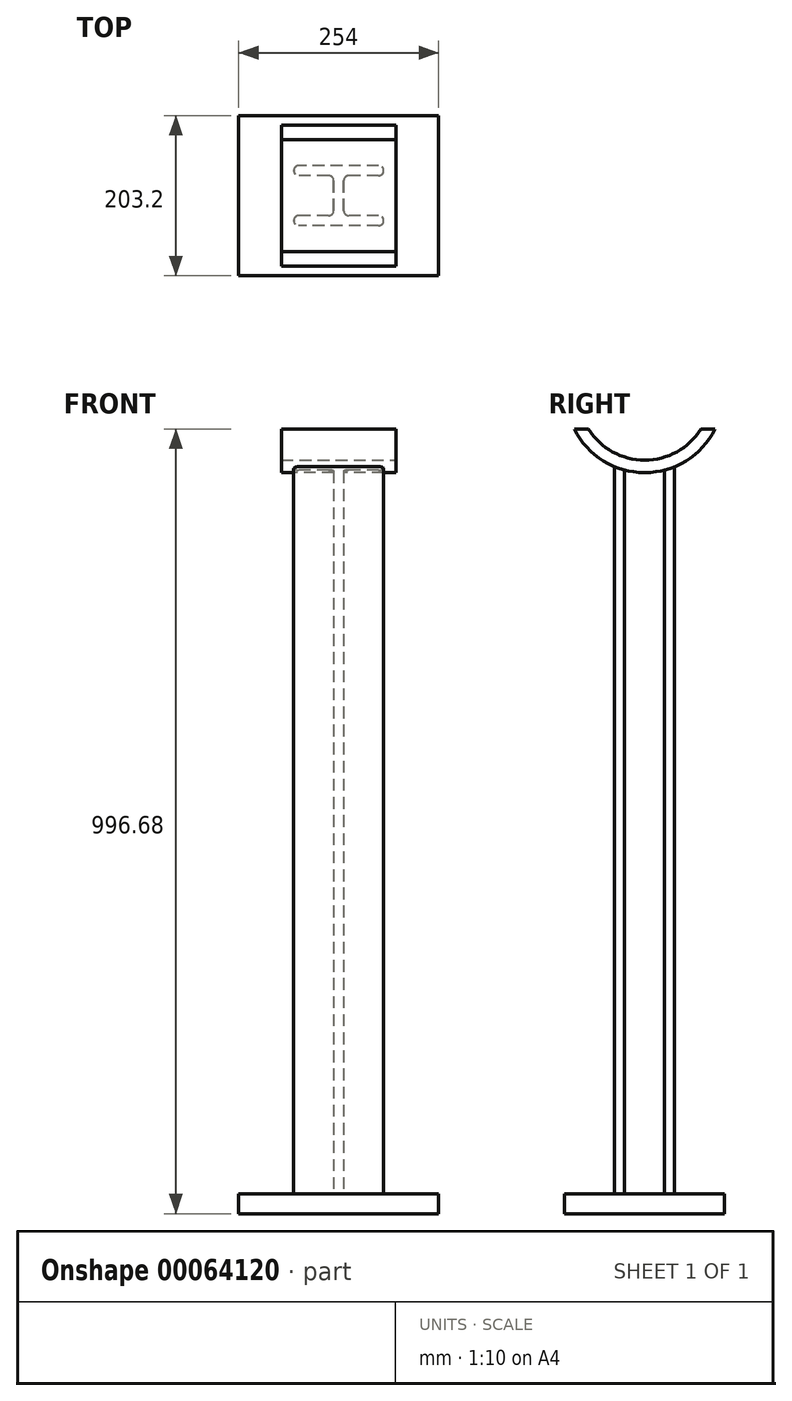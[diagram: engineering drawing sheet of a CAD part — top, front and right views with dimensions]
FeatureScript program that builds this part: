
annotation { "Feature Type Name" : "Feature", "Feature Type Description" : "" }
export const myFeature = defineFeature(function(context is Context, id is Id, definition is map)
    precondition{}
    {
        {
            var Q0;
            Q0=qCreatedBy(makeId("Top.planeOp"),FACE);
            var sketch = newSketch(context, id + "F0", { "sketchPlane" : qUnion([Q0])});
            skLineSegment(sketch, "E0.bottom", {"start": v(50.8, 38.1) * mm, "end": v(-50.8, 38.1) * mm});
            skLineSegment(sketch, "E0.top", {"start": v(50.8, -38.1) * mm, "end": v(-50.8, -38.1) * mm});
            skLineSegment(sketch, "E0.left", {"start": v(57.15, 31.75) * mm, "end": v(57.15, 31.75) * mm});
            skLineSegment(sketch, "E0.right", {"start": v(-57.15, 31.75) * mm, "end": v(-57.15, 31.75) * mm});
            skPoint(sketch, "E0.middle", {"position": v(0, 0) * mm});
            skLineSegment(sketch, "E1", {"start": v(-50.8, 25.4) * mm, "end": v(-12.7, 25.4) * mm});
            skLineSegment(sketch, "E2", {"start": v(-50.8, -25.4) * mm, "end": v(-12.7, -25.4) * mm});
            skLineSegment(sketch, "E3", {"start": v(-6.35, 19.05) * mm, "end": v(-6.35, -19.05) * mm});
            skLineSegment(sketch, "E4", {"start": v(6.35, 19.05) * mm, "end": v(6.35, -19.05) * mm});
            skLineSegment(sketch, "E5.trimOffspring", {"start": v(12.7, 25.4) * mm, "end": v(50.8, 25.4) * mm});
            skLineSegment(sketch, "E6.trimOffspring", {"start": v(-57.15, -31.75) * mm, "end": v(-57.15, -31.75) * mm});
            skLineSegment(sketch, "E7.trimOffspring", {"start": v(57.15, -31.75) * mm, "end": v(57.15, -31.75) * mm});
            skLineSegment(sketch, "E8.trimOffspring", {"start": v(12.7, -25.4) * mm, "end": v(50.8, -25.4) * mm});
            skPoint(sketch, "E9.visualSharp", {"position": v(-6.35, 25.4) * mm});
            skArc(sketch, "E9.filletArc", {"start": v(-6.35, 19.05) * mm, "mid": v(-8.2, 23.54) * mm, "end": v(-12.7, 25.4) * mm});
            skPoint(sketch, "E10.visualSharp", {"position": v(6.35, 25.4) * mm});
            skArc(sketch, "E10.filletArc", {"start": v(12.7, 25.4) * mm, "mid": v(8.2, 23.54) * mm, "end": v(6.35, 19.05) * mm});
            skPoint(sketch, "E11.visualSharp", {"position": v(-6.35, -25.4) * mm});
            skArc(sketch, "E11.filletArc", {"start": v(-12.7, -25.4) * mm, "mid": v(-8.2, -23.54) * mm, "end": v(-6.35, -19.05) * mm});
            skPoint(sketch, "E12.visualSharp", {"position": v(6.35, -25.4) * mm});
            skArc(sketch, "E12.filletArc", {"start": v(6.35, -19.05) * mm, "mid": v(8.2, -23.54) * mm, "end": v(12.7, -25.4) * mm});
            skPoint(sketch, "E13.visualSharp", {"position": v(-57.15, 25.4) * mm});
            skArc(sketch, "E13.filletArc", {"start": v(-57.15, 31.75) * mm, "mid": v(-55.3, 27.26) * mm, "end": v(-50.8, 25.4) * mm});
            skPoint(sketch, "E14.visualSharp", {"position": v(-57.15, 38.1) * mm});
            skArc(sketch, "E14.filletArc", {"start": v(-50.8, 38.1) * mm, "mid": v(-55.3, 36.24) * mm, "end": v(-57.15, 31.75) * mm});
            skPoint(sketch, "E15.visualSharp", {"position": v(57.15, 38.1) * mm});
            skArc(sketch, "E15.filletArc", {"start": v(57.15, 31.75) * mm, "mid": v(55.3, 36.24) * mm, "end": v(50.8, 38.1) * mm});
            skPoint(sketch, "E16.visualSharp", {"position": v(57.15, 25.4) * mm});
            skArc(sketch, "E16.filletArc", {"start": v(50.8, 25.4) * mm, "mid": v(55.3, 27.26) * mm, "end": v(57.15, 31.75) * mm});
            skPoint(sketch, "E17.visualSharp", {"position": v(57.15, -25.4) * mm});
            skArc(sketch, "E17.filletArc", {"start": v(57.15, -31.75) * mm, "mid": v(55.3, -27.26) * mm, "end": v(50.8, -25.4) * mm});
            skPoint(sketch, "E18.visualSharp", {"position": v(57.15, -38.1) * mm});
            skArc(sketch, "E18.filletArc", {"start": v(50.8, -38.1) * mm, "mid": v(55.3, -36.24) * mm, "end": v(57.15, -31.75) * mm});
            skPoint(sketch, "E19.visualSharp", {"position": v(-57.15, -38.1) * mm});
            skArc(sketch, "E19.filletArc", {"start": v(-57.15, -31.75) * mm, "mid": v(-55.3, -36.24) * mm, "end": v(-50.8, -38.1) * mm});
            skPoint(sketch, "E20.visualSharp", {"position": v(-57.15, -25.4) * mm});
            skArc(sketch, "E20.filletArc", {"start": v(-50.8, -25.4) * mm, "mid": v(-55.3, -27.26) * mm, "end": v(-57.15, -31.75) * mm});
            skSolve(sketch);
        }
        {
            var Q0;
            Q0=qCreatedBy(makeId("Top.planeOp"),FACE);
            var sketch = newSketch(context, id + "F1", { "sketchPlane" : qUnion([Q0])});
            skLineSegment(sketch, "E21.bottom", {"start": v(127, 101.6) * mm, "end": v(-127, 101.6) * mm});
            skLineSegment(sketch, "E21.top", {"start": v(127, -101.6) * mm, "end": v(-127, -101.6) * mm});
            skLineSegment(sketch, "E21.left", {"start": v(127, 101.6) * mm, "end": v(127, -101.6) * mm});
            skLineSegment(sketch, "E21.right", {"start": v(-127, 101.6) * mm, "end": v(-127, -101.6) * mm});
            skPoint(sketch, "E21.middle", {"position": v(0, 0) * mm});
            skSolve(sketch);
        }
        {
            var Q0;
            Q0=makeQuery(id+"F1.imprint","IMPRINT",FACE,{"disambiguationData":[TD([[makeQuery(id+"F1.imprint","IMPRINT",EDGE,{"derivedFrom":sQuery(id+"F1.wireOp",EDGE,"E21.bottom")}),1.0]])]});
            extrude(context, id + "F2", {"entities" : qUnion([Q0]), "oppositeDirection" : true, "depth" : 25.4 * mm, "offsetDistance" : 25.4 * mm});
        }
        {
            var Q0;
            Q0 = qSketchRegion(id + "F0", true);
            extrude(context, id + "F3", {"entities" : qUnion([Q0]), "operationType" : NewBodyOperationType.ADD, "depth" : 1019.05 * mm, "offsetDistance" : 25.4 * mm});
        }
        {
            var Q0;
            Q0=qCreatedBy(makeId("Right.planeOp"),FACE);
            var sketch = newSketch(context, id + "F4", { "sketchPlane" : qUnion([Q0])});
            skLineSegment(sketch, "E22", {"start": v(0, 0) * mm, "end": v(0, 1016) * mm, "construction": true});
            skCircle(sketch, "E23", {"center": v(0, 1016) * mm, "radius": 84.14 * mm});
            skArc(sketch, "E24", {"start": v(-89.4, 971.28) * mm, "mid": v(0, 916.03) * mm, "end": v(89.4, 971.28) * mm});
            skLineSegment(sketch, "E25", {"start": v(-89.4, 971.28) * mm, "end": v(-71.27, 971.28) * mm});
            skLineSegment(sketch, "E26.trimOffspring", {"start": v(71.27, 971.28) * mm, "end": v(89.4, 971.28) * mm});
            skSolve(sketch);
        }
        {
            var Q0;
            {var subQ0=sQuery(id+"F4.wireOp",EDGE,"E23");var subQ1=makeQuery(id+"F4.imprint","INTERSECT",VERTEX,{"derivedFrom":[subQ0,sQuery(id+"F4.wireOp",EDGE,"E25")]});Q0=makeQuery(id+"F4.imprint","IMPRINT",FACE,{"disambiguationData":[TD([[makeQuery(id+"F4.imprint","IMPRINT",EDGE,{"disambiguationData":[TD([[subQ1,-1.0]])],"derivedFrom":subQ0}),1.0]])]});}
            extrude(context, id + "F5", {"entities" : qUnion([Q0]), "operationType" : NewBodyOperationType.REMOVE, "oppositeDirection" : true, "depth" : 206.25 * mm, "offsetDistance" : 25.4 * mm, "symmetric" : true});
        }
        {
            var Q0;
            Q0=makeQuery(id+"F4.imprint","IMPRINT",FACE,{"disambiguationData":[TD([[makeQuery(id+"F4.imprint","IMPRINT",EDGE,{"derivedFrom":sQuery(id+"F4.wireOp",EDGE,"E24")}),1.0]])]});
            extrude(context, id + "F6", {"entities" : qUnion([Q0]), "operationType" : NewBodyOperationType.ADD, "depth" : 145.8 * mm, "offsetDistance" : 25.4 * mm, "symmetric" : true});
        }
    });
